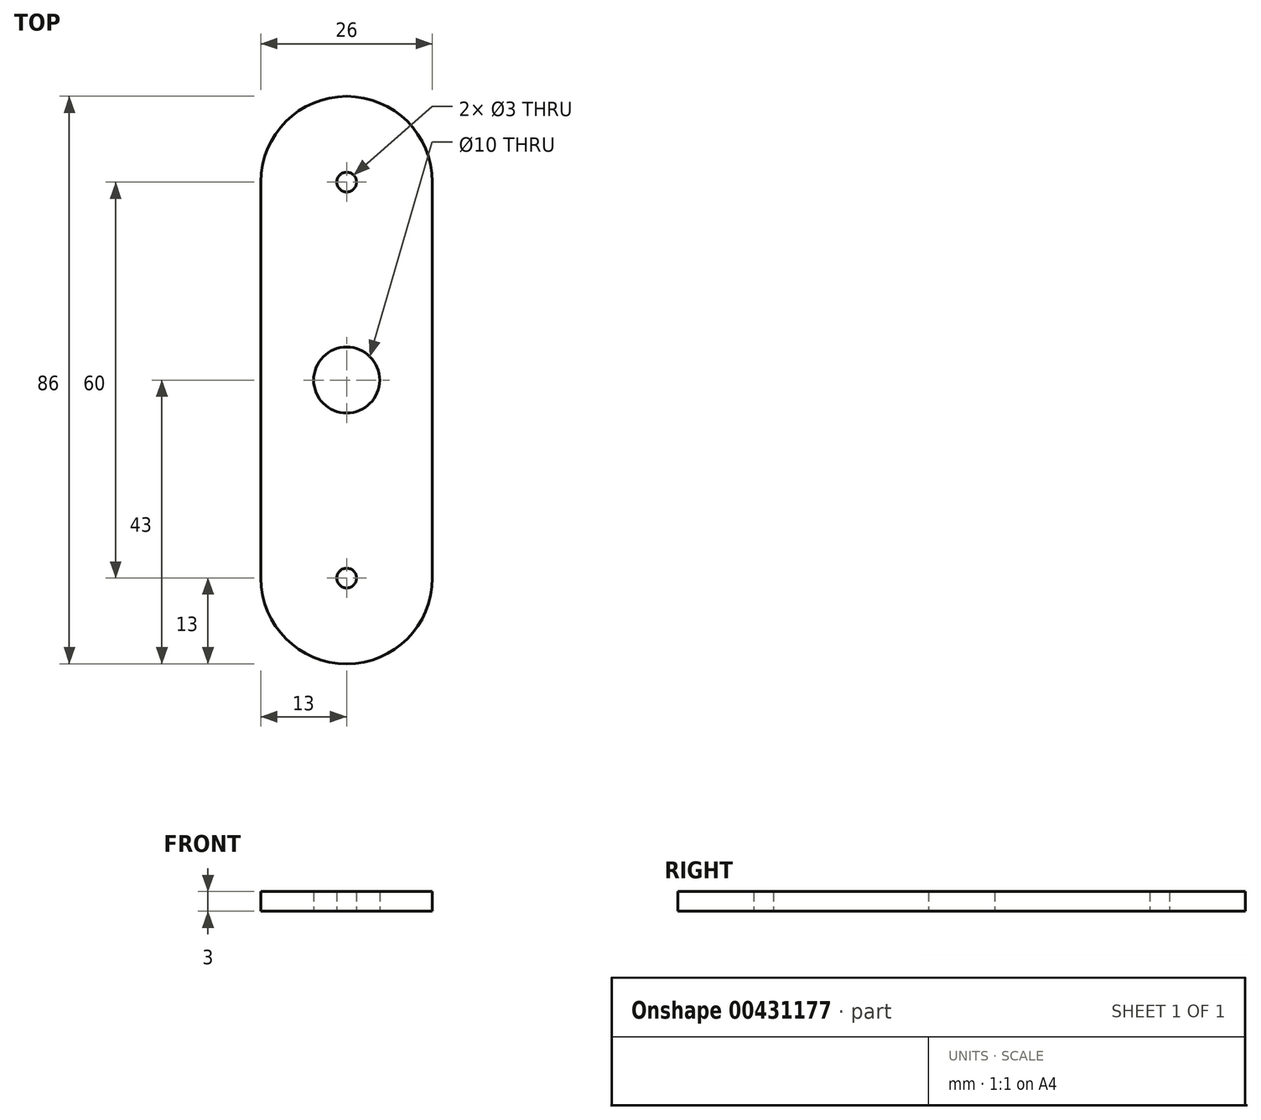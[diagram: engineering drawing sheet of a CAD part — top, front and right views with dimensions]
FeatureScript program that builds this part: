
annotation { "Feature Type Name" : "Feature", "Feature Type Description" : "" }
export const myFeature = defineFeature(function(context is Context, id is Id, definition is map)
    precondition{}
    {
        {
            var Q0;
            Q0=qCreatedBy(makeId("Top.planeOp"),FACE);
            var sketch = newSketch(context, id + "F0", { "sketchPlane" : qUnion([Q0])});
            skLineSegment(sketch, "E0", {"start": v(0, 0) * mm, "end": v(0, 30) * mm, "construction": true});
            skArc(sketch, "E1", {"start": v(13, 30) * mm, "mid": v(0, 43) * mm, "end": v(-13, 30) * mm});
            skLineSegment(sketch, "E2", {"start": v(13, 0) * mm, "end": v(13, 30) * mm});
            skLineSegment(sketch, "E3", {"start": v(-13, 0) * mm, "end": v(-13, 30) * mm});
            skCircle(sketch, "E4", {"center": v(0, 30) * mm, "radius": 1.5 * mm});
            skLineSegment(sketch, "E5.MirrorCS", {"start": v(13, 0) * mm, "end": v(13, -30) * mm});
            skArc(sketch, "E6.MirrorCS", {"start": v(13, -30) * mm, "mid": v(0, -43) * mm, "end": v(-13, -30) * mm});
            skLineSegment(sketch, "E7.MirrorCS", {"start": v(-13, 0) * mm, "end": v(-13, -30) * mm});
            skCircle(sketch, "E8.MirrorC", {"center": v(0, -30) * mm, "radius": 1.5 * mm});
            skCircle(sketch, "E9", {"center": v(0, 0) * mm, "radius": 5 * mm});
            skSolve(sketch);
        }
        {
            var Q0;
            Q0=makeQuery(id+"F0.imprint","IMPRINT",FACE,{"disambiguationData":[TD([[makeQuery(id+"F0.imprint","IMPRINT",EDGE,{"derivedFrom":sQuery(id+"F0.wireOp",EDGE,"E1")}),1.0]])]});
            extrude(context, id + "F1", {"entities" : qUnion([Q0]), "depth" : 3 * mm});
        }
    });
